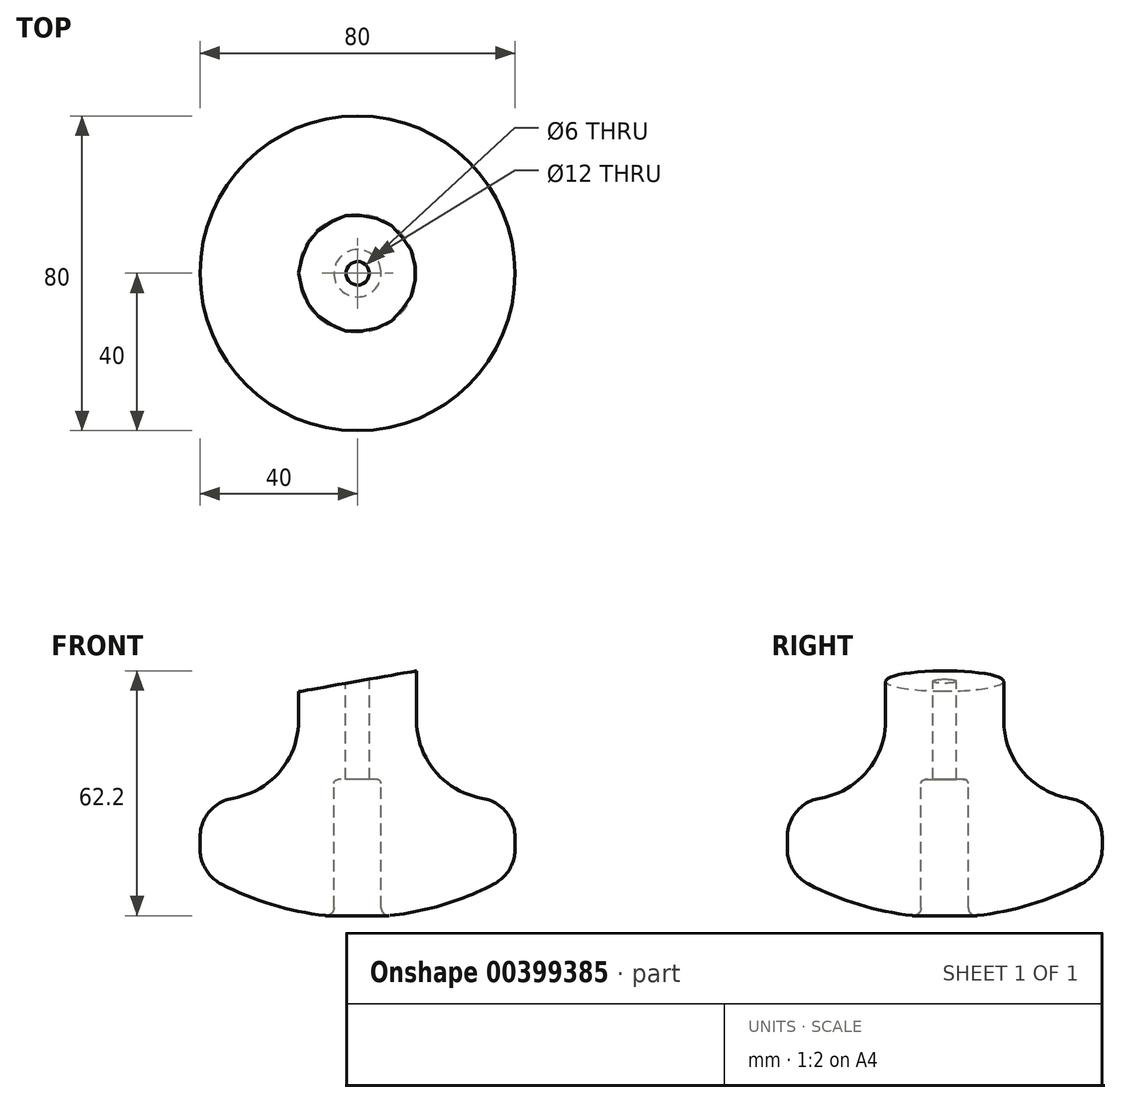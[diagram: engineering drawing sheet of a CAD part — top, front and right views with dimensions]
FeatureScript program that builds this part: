
annotation { "Feature Type Name" : "Feature", "Feature Type Description" : "" }
export const myFeature = defineFeature(function(context is Context, id is Id, definition is map)
    precondition{}
    {
        {
            var Q0;
            Q0=qCreatedBy(makeId("Front.planeOp"),FACE);
            var sketch = newSketch(context, id + "F0", { "sketchPlane" : qUnion([Q0])});
            skLineSegment(sketch, "E0", {"start": v(0, -60) * mm, "end": v(0, 0) * mm});
            skLineSegment(sketch, "E1", {"start": v(0, 0) * mm, "end": v(15, 0) * mm});
            skLineSegment(sketch, "E2", {"start": v(15, 0) * mm, "end": v(15, -30) * mm});
            skLineSegment(sketch, "E3", {"start": v(15, -30) * mm, "end": v(40, -30) * mm});
            skLineSegment(sketch, "E4", {"start": v(40, -30) * mm, "end": v(40, -48.44) * mm});
            skCircle(sketch, "E5", {"center": v(0, 15) * mm, "radius": 75 * mm});
            skLineSegment(sketch, "E6", {"start": v(15, 0) * mm, "end": v(15, 5) * mm});
            skLineSegment(sketch, "E7", {"start": v(15, 5) * mm, "end": v(0, 5) * mm});
            skLineSegment(sketch, "E8", {"start": v(0, 5) * mm, "end": v(0, 0) * mm});
            skSolve(sketch);
        }
        {
            var Q0;
            {var subQ0=sQuery(id+"F0.wireOp",EDGE,"E0");Q0=makeQuery(id+"F0.imprint","IMPRINT",FACE,{"disambiguationData":[TD([[makeQuery(id+"F0.imprint","IMPRINT",EDGE,{"derivedFrom":subQ0}),-1.0]])]});}
            var Q1;
            Q1=makeQuery(id+"F0.imprint","IMPRINT",FACE,{"disambiguationData":[TD([[makeQuery(id+"F0.imprint","IMPRINT",EDGE,{"derivedFrom":sQuery(id+"F0.wireOp",EDGE,"E1")}),1.0]])]});
            var Q2;
            Q2=sQuery(id+"F0.wireOp",EDGE,"E0");
            revolve(context, id + "F1", {"entities" : qUnion([Q0, Q1]), "axis" : qUnion([Q2]), "revolveType" : RevolveType.FULL});
        }
        {
            var Q0;
            Q0=makeQuery(id+"F1.opRevolve","SWEPT_EDGE",EDGE,{"disambiguationData":[OSD([sQuery(id+"F0.wireOp",EDGE,"E2"),sQuery(id+"F0.wireOp",EDGE,"E3")])]});
            fillet(context, id + "F2", {"entities" : qUnion([Q0]), "radius" : 20 * mm, "tangentPropagation" : true, "allowEdgeOverflow" : false});
        }
        {
            var Q0;
            Q0=makeQuery(id+"F1.opRevolve","SWEPT_EDGE",EDGE,{"disambiguationData":[OSD([sQuery(id+"F0.wireOp",EDGE,"E4"),sQuery(id+"F0.wireOp",EDGE,"E5")])]});
            var Q1;
            Q1=makeQuery(id+"F1.opRevolve","SWEPT_EDGE",EDGE,{"disambiguationData":[OSD([sQuery(id+"F0.wireOp",EDGE,"E3"),sQuery(id+"F0.wireOp",EDGE,"E4")])]});
            fillet(context, id + "F3", {"entities" : qUnion([Q0, Q1]), "radius" : 10 * mm, "tangentPropagation" : true, "allowEdgeOverflow" : false});
        }
        {
            var Q0;
            Q0=qCreatedBy(makeId("Top.planeOp"),FACE);
            var sketch = newSketch(context, id + "F4", { "sketchPlane" : qUnion([Q0])});
            skCircle(sketch, "E9", {"center": v(0, 0) * mm, "radius": 3 * mm});
            skSolve(sketch);
        }
        {
            var Q0;
            Q0=makeQuery(id+"F4.imprint","IMPRINT",FACE,{"disambiguationData":[TD([[makeQuery(id+"F4.imprint","IMPRINT",EDGE,{"derivedFrom":sQuery(id+"F4.wireOp",EDGE,"E9")}),1.0]])]});
            extrude(context, id + "F5", {"entities" : qUnion([Q0]), "operationType" : NewBodyOperationType.REMOVE, "endBound" : BoundingType.SYMMETRIC, "oppositeDirection" : true, "depth" : 200 * mm});
        }
        {
            var Q0;
            Q0=qCreatedBy(makeId("Top.planeOp"),FACE);
            var sketch = newSketch(context, id + "F6", { "sketchPlane" : qUnion([Q0])});
            skCircle(sketch, "E10", {"center": v(0, 0) * mm, "radius": 6 * mm});
            skSolve(sketch);
        }
        {
            var Q0;
            Q0=makeQuery(id+"F6.imprint","IMPRINT",FACE,{"disambiguationData":[TD([[makeQuery(id+"F6.imprint","IMPRINT",EDGE,{"derivedFrom":sQuery(id+"F6.wireOp",EDGE,"E10")}),1.0]])]});
            extrude(context, id + "F7", {"entities" : qUnion([Q0]), "operationType" : NewBodyOperationType.REMOVE, "oppositeDirection" : true, "depth" : 100 * mm, "hasSecondDirection" : true, "secondDirectionOppositeDirection" : true, "secondDirectionDepth" : 25 * mm});
        }
        {
            var Q0;
            Q0=makeQuery(id+"F7.boolean.opBoolean","COPY",EDGE,{"derivedFrom":makeQuery(id+"F7.opExtrude","CAP_EDGE",EDGE,{"disambiguationData":[OSD([sQuery(id+"F6.wireOp",EDGE,"E10")])],"isStart":true})});
            fillet(context, id + "F8", {"entities" : qUnion([Q0]), "radius" : 1 * mm, "tangentPropagation" : true, "allowEdgeOverflow" : false});
        }
        {
            var Q0;
            Q0=makeQuery(id+"F7.boolean.opBoolean","INTERSECT",EDGE,{"derivedFrom":[makeQuery(id+"F1.opRevolve","SWEPT_FACE",FACE,{"disambiguationData":[OSD([sQuery(id+"F0.wireOp",EDGE,"E5")])]}),makeQuery(id+"F7.opExtrude","SWEPT_FACE",FACE,{"disambiguationData":[OSD([sQuery(id+"F6.wireOp",EDGE,"E10")])]})]});
            fillet(context, id + "F9", {"entities" : qUnion([Q0]), "radius" : 2 * mm, "tangentPropagation" : true, "allowEdgeOverflow" : false});
        }
        {
            var Q0;
            Q0=qCreatedBy(makeId("Front.planeOp"),FACE);
            var sketch = newSketch(context, id + "F10", { "sketchPlane" : qUnion([Q0])});
            skLineSegment(sketch, "E11", {"start": v(50, 8.82) * mm, "end": v(-50, -8.82) * mm});
            skLineSegment(sketch, "E12", {"start": v(-50, -8.82) * mm, "end": v(-50, 8.82) * mm});
            skLineSegment(sketch, "E13", {"start": v(-50, 8.82) * mm, "end": v(50, 8.82) * mm});
            skSolve(sketch);
        }
        {
            var Q0;
            Q0=makeQuery(id+"F10.imprint","IMPRINT",FACE,{"disambiguationData":[TD([[makeQuery(id+"F10.imprint","IMPRINT",EDGE,{"derivedFrom":sQuery(id+"F10.wireOp",EDGE,"E11")}),-1.0]])]});
            extrude(context, id + "F11", {"entities" : qUnion([Q0]), "operationType" : NewBodyOperationType.REMOVE, "endBound" : BoundingType.SYMMETRIC, "oppositeDirection" : true, "depth" : 50 * mm});
        }
    });
